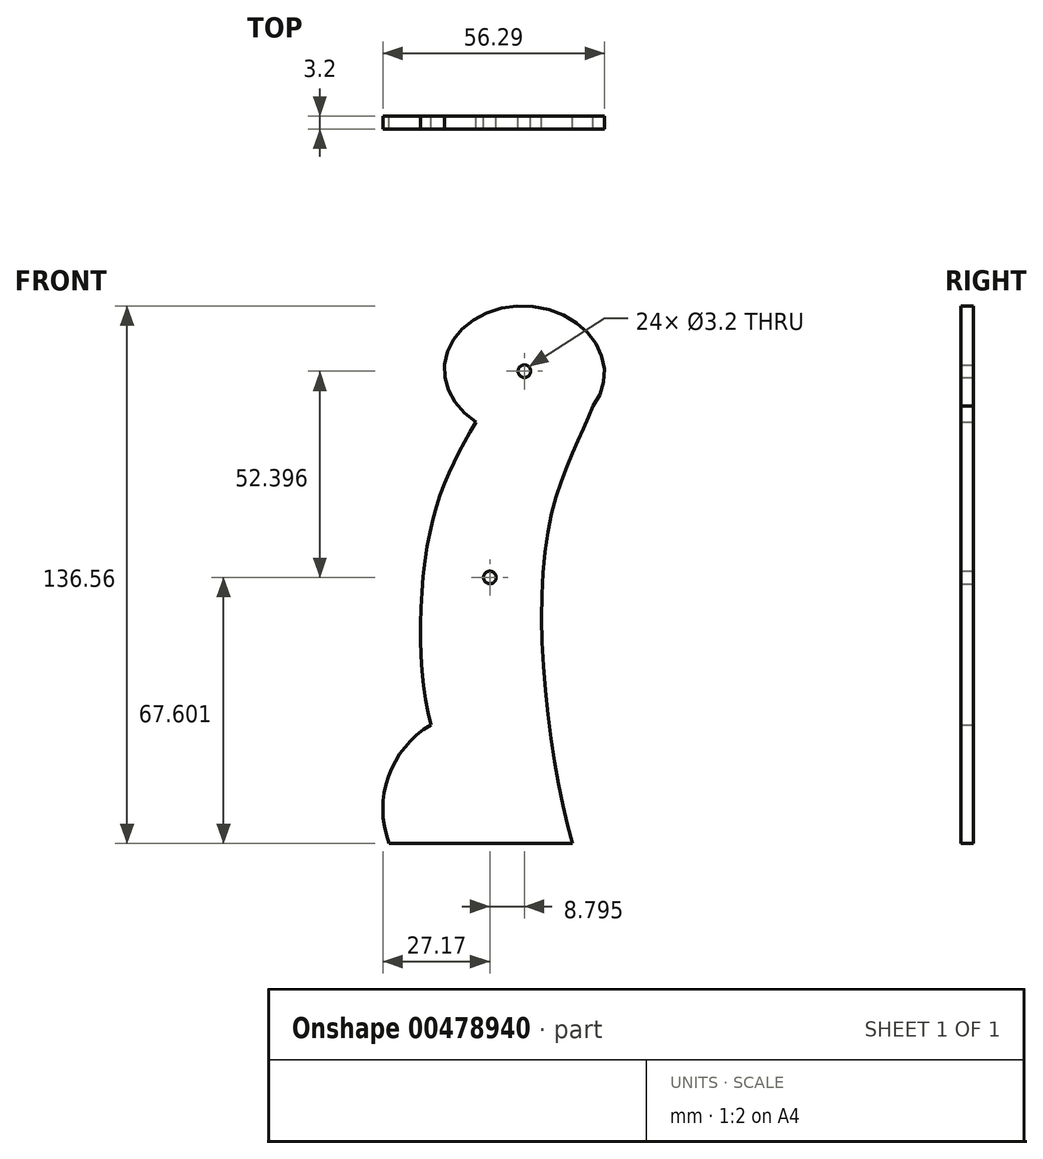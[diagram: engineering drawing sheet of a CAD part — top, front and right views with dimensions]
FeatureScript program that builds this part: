
annotation { "Feature Type Name" : "Feature", "Feature Type Description" : "" }
export const myFeature = defineFeature(function(context is Context, id is Id, definition is map)
    precondition{}
    {
        {
            var Q0;
            Q0=qCreatedBy(makeId("Front.planeOp"),FACE);
            var sketch = newSketch(context, id + "F0", { "sketchPlane" : qUnion([Q0])});
            skFitSpline(sketch, "E0", {"points": [v(21.04, -48.38) * mm, v(14.57, 29.7) * mm, v(26.23, 62.74) * mm], "startDerivative": vector(-29.97, 102.2) * mm, "endDerivative": vector(24.04, 62.9) * mm});
            skFitSpline(sketch, "E1", {"points": [v(-14.94, -18.2) * mm, v(-15.43, 29.7) * mm, v(-3.5, 58.68) * mm], "startDerivative": vector(-18.97, 67.17) * mm, "endDerivative": vector(35.56, 58.6) * mm});
            skLineSegment(sketch, "E2", {"start": v(21.04, -48.38) * mm, "end": v(-25.58, -48.38) * mm});
            skArc(sketch, "E3", {"start": v(-25.58, -48.38) * mm, "mid": v(-25.75, -31.36) * mm, "end": v(-14.95, -18.2) * mm});
            skPoint(sketch, "E3.centerSnap0", {"position": v(-2.27, -48.38) * mm});
            skEllipse(sketch, "E4", {"center": v(8.8, 71.62) * mm, "majorRadius": 20.34 * mm, "minorRadius": 16.55 * mm, "majorAxis": v(-1, 0.06)});
            skCircle(sketch, "E5", {"center": v(0, 19.22) * mm, "radius": 1.6 * mm});
            skCircle(sketch, "E6", {"center": v(8.8, 71.62) * mm, "radius": 1.6 * mm});
            skSolve(sketch);
        }
        {
            var Q0;
            Q0 = qSketchRegion(id + "F0", true);
            extrude(context, id + "F1", {"entities" : qUnion([Q0]), "depth" : 3.2 * mm, "offsetDistance" : 25 * mm});
        }
        {
            var Q0;
            Q0=makeQuery(id+"F0.imprint","IMPRINT",FACE,{"disambiguationData":[TD([[makeQuery(id+"F0.imprint","IMPRINT",EDGE,{"derivedFrom":sQuery(id+"F0.wireOp",EDGE,"E6")}),1.0]])]});
            var Q1;
            Q1=makeQuery(id+"F0.imprint","IMPRINT",FACE,{"disambiguationData":[TD([[makeQuery(id+"F0.imprint","IMPRINT",EDGE,{"derivedFrom":sQuery(id+"F0.wireOp",EDGE,"E5")}),1.0]])]});
            extrude(context, id + "F2", {"entities" : qUnion([Q0, Q1]), "operationType" : NewBodyOperationType.REMOVE, "endBound" : BoundingType.THROUGH_ALL, "depth" : 25 * mm, "offsetDistance" : 25 * mm});
        }
    });
